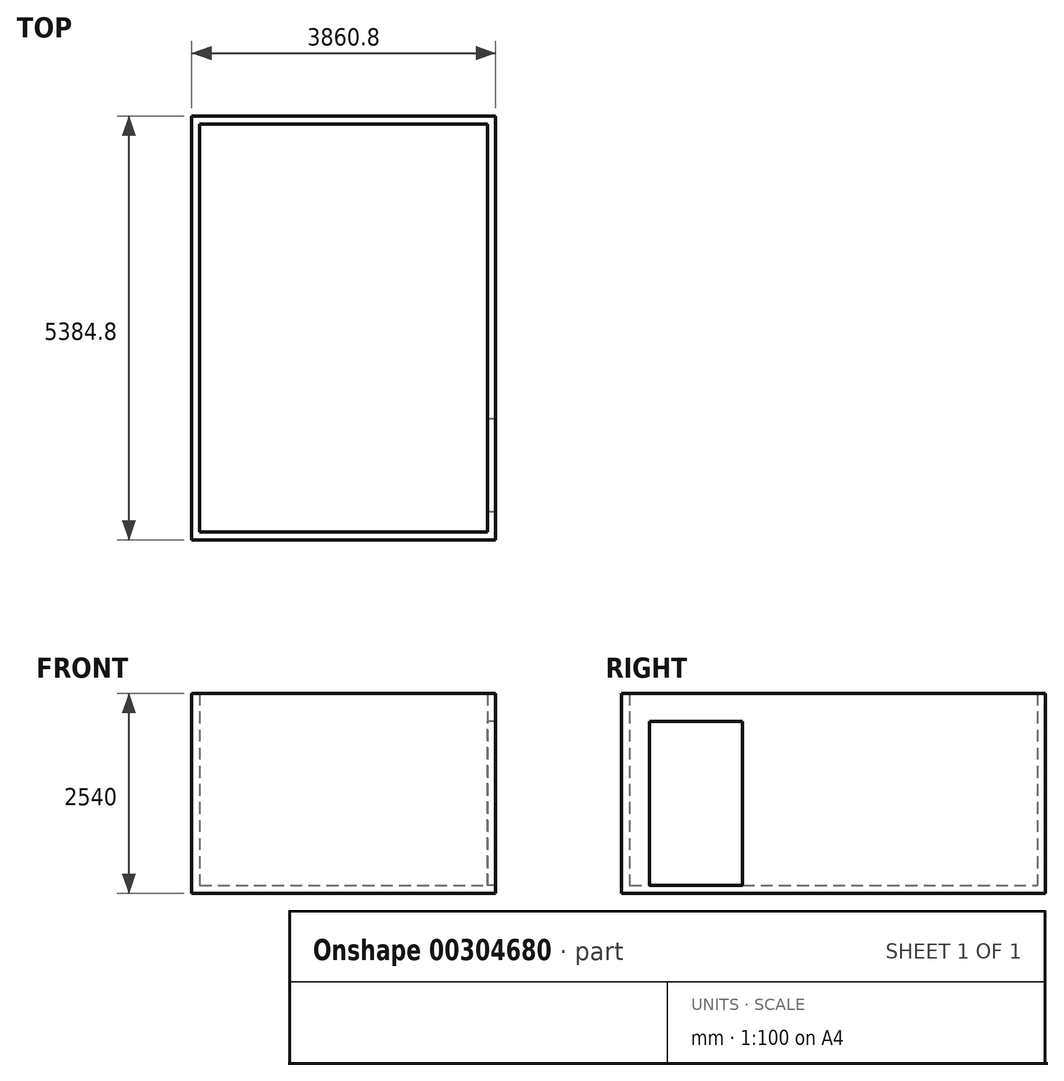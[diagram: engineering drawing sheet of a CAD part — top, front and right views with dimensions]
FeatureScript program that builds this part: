
annotation { "Feature Type Name" : "Feature", "Feature Type Description" : "" }
export const myFeature = defineFeature(function(context is Context, id is Id, definition is map)
    precondition{}
    {
        {
            var Q0;
            Q0=qCreatedBy(makeId("Top.planeOp"),FACE);
            var sketch = newSketch(context, id + "F0", { "sketchPlane" : qUnion([Q0])});
            skLineSegment(sketch, "E0.bottom", {"start": v(-2883.49, 1369.88) * mm, "end": v(774.11, 1369.88) * mm});
            skLineSegment(sketch, "E0.top", {"start": v(-2883.49, -3811.72) * mm, "end": v(774.11, -3811.72) * mm});
            skLineSegment(sketch, "E0.left", {"start": v(-2883.49, 1369.88) * mm, "end": v(-2883.49, -3811.72) * mm});
            skLineSegment(sketch, "E0.right", {"start": v(774.11, 1369.88) * mm, "end": v(774.11, -3811.72) * mm});
            skLineSegment(sketch, "E1.bottom", {"start": v(-2985.09, 1471.48) * mm, "end": v(875.71, 1471.48) * mm});
            skLineSegment(sketch, "E1.top", {"start": v(-2985.09, -3913.32) * mm, "end": v(875.71, -3913.32) * mm});
            skLineSegment(sketch, "E1.left", {"start": v(-2985.09, 1471.48) * mm, "end": v(-2985.09, -3913.32) * mm});
            skLineSegment(sketch, "E1.right", {"start": v(875.71, 1471.48) * mm, "end": v(875.71, -3913.32) * mm});
            skSolve(sketch);
        }
        {
            var Q0;
            Q0=makeQuery(id+"F0.imprint","IMPRINT",FACE,{"disambiguationData":[TD([[makeQuery(id+"F0.imprint","IMPRINT",EDGE,{"derivedFrom":sQuery(id+"F0.wireOp",EDGE,"E0.bottom")}),1.0]])]});
            extrude(context, id + "F1", {"entities" : qUnion([Q0]), "depth" : 2540 * mm});
        }
        {
            var Q0;
            Q0=makeQuery(id+"F1.opExtrude","SWEPT_FACE",FACE,{"disambiguationData":[OSD([sQuery(id+"F0.wireOp",EDGE,"E0.right")])]});
            var sketch = newSketch(context, id + "F2", { "sketchPlane" : qUnion([Q0])});
            skLineSegment(sketch, "E2.bottom", {"start": v(3811.72, 0) * mm, "end": v(-1369.88, 0) * mm});
            skLineSegment(sketch, "E2.top", {"start": v(3811.72, 101.6) * mm, "end": v(-1369.88, 101.6) * mm});
            skLineSegment(sketch, "E2.left", {"start": v(3811.72, 0) * mm, "end": v(3811.72, 101.6) * mm});
            skLineSegment(sketch, "E2.right", {"start": v(-1369.88, 0) * mm, "end": v(-1369.88, 101.6) * mm});
            skSolve(sketch);
        }
        {
            var Q0;
            Q0=makeQuery(id+"F2.imprint","IMPRINT",FACE,{"disambiguationData":[TD([[makeQuery(id+"F2.imprint","IMPRINT",EDGE,{"derivedFrom":sQuery(id+"F2.wireOp",EDGE,"E2.bottom")}),1.0]])]});
            var Q1;
            Q1=makeQuery(id+"F1.opExtrude","SWEPT_FACE",FACE,{"disambiguationData":[OSD([sQuery(id+"F0.wireOp",EDGE,"E0.left")])]});
            extrude(context, id + "F3", {"entities" : qUnion([Q0]), "operationType" : NewBodyOperationType.ADD, "endBound" : BoundingType.UP_TO_SURFACE, "endBoundEntityFace" : qUnion([Q1]), "depth" : 25.4 * mm});
        }
        {
            var Q0;
            Q0=makeQuery(id+"F1.opExtrude","SWEPT_FACE",FACE,{"disambiguationData":[OSD([sQuery(id+"F0.wireOp",EDGE,"E0.right")])]});
            var sketch = newSketch(context, id + "F4", { "sketchPlane" : qUnion([Q0])});
            skLineSegment(sketch, "E3.bottom", {"start": v(3557.72, 101.6) * mm, "end": v(2376.62, 101.6) * mm});
            skLineSegment(sketch, "E3.top", {"start": v(3557.72, 2184.4) * mm, "end": v(2376.62, 2184.4) * mm});
            skLineSegment(sketch, "E3.left", {"start": v(3557.72, 101.6) * mm, "end": v(3557.72, 2184.4) * mm});
            skLineSegment(sketch, "E3.right", {"start": v(2376.62, 101.6) * mm, "end": v(2376.62, 2184.4) * mm});
            skSolve(sketch);
        }
        {
            var Q0;
            Q0=makeQuery(id+"F4.imprint","IMPRINT",FACE,{"disambiguationData":[TD([[makeQuery(id+"F4.imprint","IMPRINT",EDGE,{"derivedFrom":sQuery(id+"F4.wireOp",EDGE,"E3.bottom")}),-1.0]])]});
            extrude(context, id + "F5", {"entities" : qUnion([Q0]), "operationType" : NewBodyOperationType.REMOVE, "endBound" : BoundingType.THROUGH_ALL, "oppositeDirection" : true, "depth" : 101.6 * mm});
        }
    });
